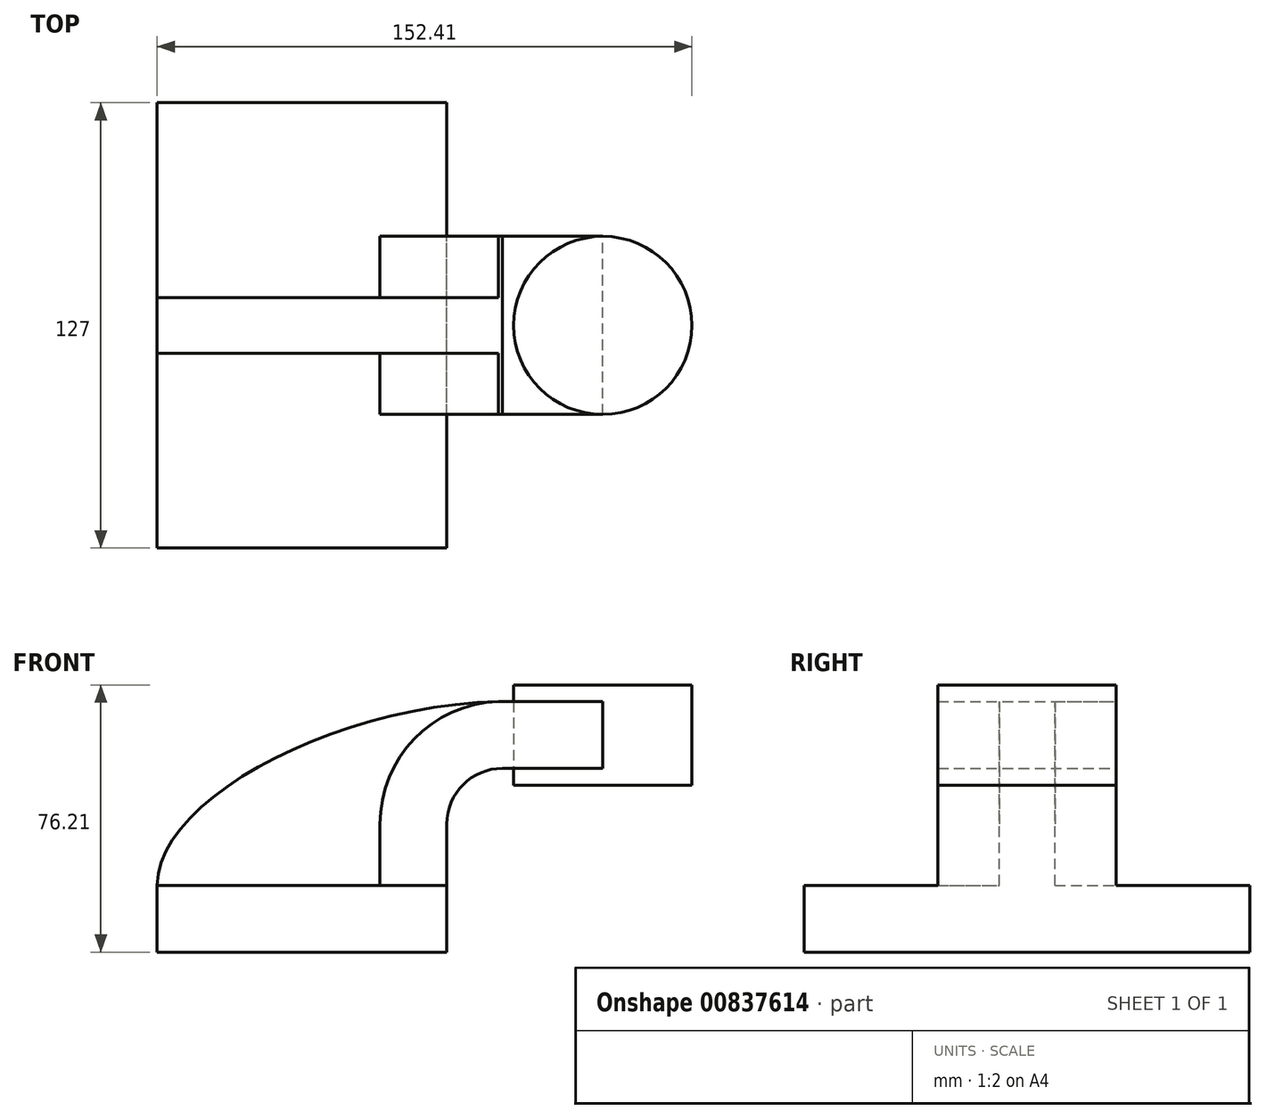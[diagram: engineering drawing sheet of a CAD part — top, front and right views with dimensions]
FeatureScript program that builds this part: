
annotation { "Feature Type Name" : "Feature", "Feature Type Description" : "" }
export const myFeature = defineFeature(function(context is Context, id is Id, definition is map)
    precondition{}
    {
        {
            var Q0;
            Q0=qCreatedBy(makeId("Front.planeOp"),FACE);
            var sketch = newSketch(context, id + "F0", { "sketchPlane" : qUnion([Q0])});
            skLineSegment(sketch, "E0.bottom", {"start": v(-41.28, 9.52) * mm, "end": v(41.27, 9.53) * mm});
            skLineSegment(sketch, "E0.top", {"start": v(-41.28, -9.53) * mm, "end": v(41.28, -9.53) * mm});
            skLineSegment(sketch, "E0.left", {"start": v(-41.28, 9.52) * mm, "end": v(-41.28, -9.53) * mm});
            skLineSegment(sketch, "E0.right", {"start": v(41.27, 9.53) * mm, "end": v(41.28, -9.52) * mm});
            skPoint(sketch, "E0.middle", {"position": v(0, 0) * mm});
            skLineSegment(sketch, "E1.bottom", {"start": v(60.32, 38.1) * mm, "end": v(111.12, 38.1) * mm});
            skLineSegment(sketch, "E1.top", {"start": v(60.32, 66.68) * mm, "end": v(111.12, 66.68) * mm});
            skLineSegment(sketch, "E1.left", {"start": v(60.32, 38.1) * mm, "end": v(60.32, 66.68) * mm});
            skLineSegment(sketch, "E1.right", {"start": v(111.12, 38.1) * mm, "end": v(111.12, 66.68) * mm});
            skPoint(sketch, "E1.middle", {"position": v(85.72, 52.39) * mm});
            skLineSegment(sketch, "E2", {"start": v(41.27, 9.53) * mm, "end": v(41.27, 27) * mm});
            skArc(sketch, "E3", {"start": v(41.27, 27) * mm, "mid": v(45.92, 38.23) * mm, "end": v(57.15, 42.88) * mm});
            skLineSegment(sketch, "E4", {"start": v(57.15, 42.88) * mm, "end": v(85.72, 42.88) * mm});
            skLineSegment(sketch, "E5.0", {"start": v(57.15, 61.93) * mm, "end": v(85.72, 61.93) * mm});
            skArc(sketch, "E5.1", {"start": v(22.22, 27) * mm, "mid": v(32.45, 51.7) * mm, "end": v(57.15, 61.93) * mm});
            skLineSegment(sketch, "E5.2", {"start": v(22.22, 9.53) * mm, "end": v(22.22, 27) * mm});
            skFitSpline(sketch, "E6", {"points": [v(-41.28, 9.52) * mm, v(57.15, 61.93) * mm], "startDerivative": vector(0.23, 74.34) * mm, "endDerivative": vector(140.7, 1.78) * mm});
            skPoint(sketch, "E7", {"position": v(85.72, 66.68) * mm});
            skLineSegment(sketch, "E8", {"start": v(85.72, 42.88) * mm, "end": v(85.72, 66.68) * mm});
            skLineSegment(sketch, "E9", {"start": v(85.72, 42.88) * mm, "end": v(85.72, 38.1) * mm});
            skSolve(sketch);
        }
        {
            var Q0;
            Q0=makeQuery(id+"F0.imprint","IMPRINT",FACE,{"disambiguationData":[TD([[makeQuery(id+"F0.imprint","IMPRINT",EDGE,{"derivedFrom":sQuery(id+"F0.wireOp",EDGE,"E0.top")}),1.0]])]});
            extrude(context, id + "F1", {"entities" : qUnion([Q0]), "endBound" : BoundingType.SYMMETRIC, "depth" : 127 * mm, "offsetDistance" : 25.4 * mm});
        }
        {
            var Q0;
            {var subQ3=sQuery(id+"F0.wireOp",EDGE,"E5.2");Q0=makeQuery(id+"F0.imprint","IMPRINT",FACE,{"disambiguationData":[TD([[makeQuery(id+"F0.imprint","IMPRINT",EDGE,{"derivedFrom":subQ3}),1.0]])]});}
            extrude(context, id + "F2", {"entities" : qUnion([Q0]), "operationType" : NewBodyOperationType.ADD, "endBound" : BoundingType.SYMMETRIC, "depth" : 15.88 * mm, "offsetDistance" : 25.4 * mm});
        }
        {
            var Q0;
            {var subQ0=sQuery(id+"F0.wireOp",EDGE,"E4");var subQ1=sQuery(id+"F0.wireOp",EDGE,"E1.left");var subQ2=makeQuery(id+"F0.imprint","INTERSECT",VERTEX,{"derivedFrom":[subQ1,subQ0]});Q0=makeQuery(id+"F0.imprint","IMPRINT",FACE,{"disambiguationData":[TD([[makeQuery(id+"F0.imprint","IMPRINT",EDGE,{"disambiguationData":[TD([[subQ2,-1.0]])],"derivedFrom":subQ1}),-1.0]])]});}
            var Q1;
            {var subQ1=sQuery(id+"F0.wireOp",EDGE,"E2");Q1=makeQuery(id+"F0.imprint","IMPRINT",FACE,{"disambiguationData":[TD([[makeQuery(id+"F0.imprint","IMPRINT",EDGE,{"derivedFrom":subQ1}),1.0]])]});}
            extrude(context, id + "F3", {"entities" : qUnion([Q0, Q1]), "operationType" : NewBodyOperationType.ADD, "endBound" : BoundingType.SYMMETRIC, "depth" : 50.8 * mm, "offsetDistance" : 25.4 * mm});
        }
        {
            var Q0;
            {var subQ3=sQuery(id+"F0.wireOp",EDGE,"E1.right");Q0=makeQuery(id+"F0.imprint","IMPRINT",FACE,{"disambiguationData":[TD([[makeQuery(id+"F0.imprint","IMPRINT",EDGE,{"derivedFrom":subQ3}),1.0]])]});}
            var Q1;
            Q1=sQuery(id+"F0.wireOp",EDGE,"E8");
            revolve(context, id + "F4", {"surfaceOperationType" : NewSurfaceOperationType.NEW, "entities" : qUnion([Q0]), "axis" : qUnion([Q1]), "revolveType" : RevolveType.FULL});
        }
    });
